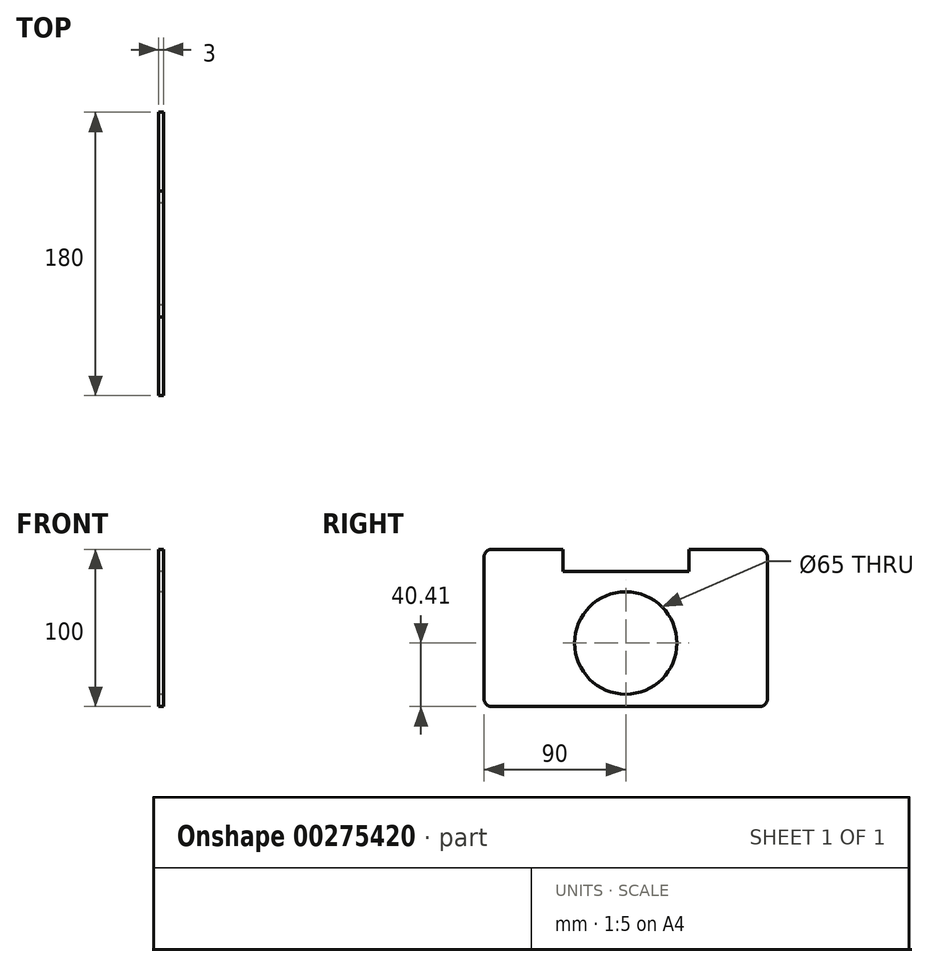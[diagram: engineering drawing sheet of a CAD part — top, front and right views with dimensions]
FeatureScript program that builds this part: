
annotation { "Feature Type Name" : "Feature", "Feature Type Description" : "" }
export const myFeature = defineFeature(function(context is Context, id is Id, definition is map)
    precondition{}
    {
        {
            var Q0;
            Q0=qCreatedBy(makeId("Right.planeOp"),FACE);
            var sketch = newSketch(context, id + "F0", { "sketchPlane" : qUnion([Q0])});
            skLineSegment(sketch, "E0.bottom", {"start": v(85, 59.59) * mm, "end": v(40, 59.59) * mm});
            skLineSegment(sketch, "E0.top", {"start": v(85, -40.41) * mm, "end": v(-85, -40.41) * mm});
            skLineSegment(sketch, "E0.left", {"start": v(90, 54.59) * mm, "end": v(90, -35.41) * mm});
            skLineSegment(sketch, "E0.right", {"start": v(-90, 54.59) * mm, "end": v(-90, -35.41) * mm});
            skPoint(sketch, "E1.visualSharp", {"position": v(90, 59.59) * mm});
            skArc(sketch, "E1.filletArc", {"start": v(90, 54.59) * mm, "mid": v(88.54, 58.12) * mm, "end": v(85, 59.59) * mm});
            skPoint(sketch, "E2.visualSharp", {"position": v(90, -40.41) * mm});
            skArc(sketch, "E2.filletArc", {"start": v(85, -40.41) * mm, "mid": v(88.54, -38.95) * mm, "end": v(90, -35.41) * mm});
            skPoint(sketch, "E3.visualSharp", {"position": v(-90, -40.41) * mm});
            skArc(sketch, "E3.filletArc", {"start": v(-90, -35.41) * mm, "mid": v(-88.54, -38.95) * mm, "end": v(-85, -40.41) * mm});
            skPoint(sketch, "E4.visualSharp", {"position": v(-90, 59.59) * mm});
            skArc(sketch, "E4.filletArc", {"start": v(-85, 59.59) * mm, "mid": v(-88.54, 58.12) * mm, "end": v(-90, 54.59) * mm});
            skLineSegment(sketch, "E5.top", {"start": v(40, 45.59) * mm, "end": v(-40, 45.59) * mm});
            skLineSegment(sketch, "E5.left", {"start": v(40, 54.59) * mm, "end": v(40, 45.59) * mm});
            skLineSegment(sketch, "E5.right", {"start": v(-40, 54.59) * mm, "end": v(-40, 45.59) * mm});
            skCircle(sketch, "E6", {"center": v(0, 0) * mm, "radius": 32.5 * mm});
            skLineSegment(sketch, "E7.trimOffspring", {"start": v(-40, 59.59) * mm, "end": v(-85, 59.59) * mm});
            skPoint(sketch, "E8.visualSharp", {"position": v(40, 59.59) * mm});
            skPoint(sketch, "E9.visualSharp", {"position": v(-40, 59.59) * mm});
            skLineSegment(sketch, "E10", {"start": v(-40, 59.59) * mm, "end": v(-40, 59.59) * mm});
            skLineSegment(sketch, "E11", {"start": v(-40, 54.59) * mm, "end": v(-40, 59.59) * mm});
            skLineSegment(sketch, "E12", {"start": v(40, 54.59) * mm, "end": v(40, 59.59) * mm});
            skLineSegment(sketch, "E13", {"start": v(40, 59.59) * mm, "end": v(40, 59.59) * mm});
            skSolve(sketch);
        }
        {
            var Q0;
            Q0=makeQuery(id+"F0.imprint","IMPRINT",FACE,{"disambiguationData":[TD([[makeQuery(id+"F0.imprint","IMPRINT",EDGE,{"derivedFrom":sQuery(id+"F0.wireOp",EDGE,"E0.bottom")}),1.0]])]});
            extrude(context, id + "F1", {"entities" : qUnion([Q0]), "depth" : 3 * mm});
        }
    });
